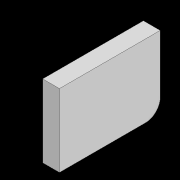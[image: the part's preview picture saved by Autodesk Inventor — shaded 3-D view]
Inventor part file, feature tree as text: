
AUTODESK INVENTOR PART (.ipt)
format: ipt  version: 2022 (Build 260153000, 153)  size: 340,480 bytes
history: native  units: in
note: dims shown in document units (in); Inventor stores cm internally (conversion verified against a paired STEP export)
features: fillet x6, extrude x5, sketch x4, projected_geometry x2
ambient origin geometry x8: Origin, YZ Plane, XZ Plane, XY Plane, X Axis, Y Axis, Z Axis, Center Point
bodies: Solid1 (feature_tree)
feature tree (17):
  extrude  "Extrusion1"  Depth=0.1575in
  extrude  "Extrusion2"  Depth=0.7874in
  extrude  "Extrusion3"  Depth=0.1575in
  fillet  "Fillet1"  Radius=0.1575in
  fillet  "Fillet2"  Radius=0.7874in
  fillet  "Fillet3"  Radius=0.1575in
  fillet  "Fillet4"  Radius=0.7874in
  sketch  "Sketch4"  dims[d26=0.7874in d27=0.1575in d28=0.7874in d30=0.1575in d31=0.7874in d32=1.378in d33=0.1575in d34=0.7874in d35=2.2441in d36=0.0in d37=0.1575in d38=0.0in d39=0.0787in d40=0.8661in d41=0.3937in d42=0.3937in d43=1.811in d44=1.811in d45=2.1457in d46=1.2303in d47=2.5591in d48=1.2795in d49=0.1575in d50=0.0in d51=1.6142in d52=1.6142in d53=0.315in d54=0.0in d58=0.0787in d59=0.9449in]
  extrude  "Extrusion4"  Depth=0.1575in
  extrude  "Extrusion5"  Depth=0.7874in
  fillet  "Fillet8"  Radius=0.1575in
  fillet  "Fillet9"  Radius=0.7874in
  sketch  "Sketch1"  dims[d10=6.4961in d11=0.1575in]
  sketch  "Sketch2"  dims[d12=4.685in d13=0.0in d18=0.7874in]
  sketch  "Sketch3"  dims[d19=0.1575in d20=0.1575in d21=0.1575in d22=0.7874in d24=0.1575in d25=0.7874in]
  projected_geometry  "Projected Loop1"
  projected_geometry  "Projected Loop2"
